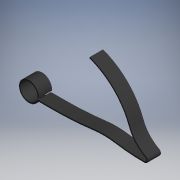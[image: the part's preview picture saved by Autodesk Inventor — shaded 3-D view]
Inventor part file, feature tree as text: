
AUTODESK INVENTOR PART (.ipt)
format: ipt  version: 2019 (Build 230136000, 136)  size: 154,624 bytes
history: native  units: mm (DEFAULTED — no unit token found)
features: extrude x1, sketch x1
ambient origin geometry x8: Origin, YZ Plane, XZ Plane, XY Plane, X Axis, Y Axis, Z Axis, Center Point
bodies: Solid1 (feature_tree)
feature tree (2):
  extrude  "Extrusion2"  Depth=1.3mm
  sketch  "Sketch1"  dims[d25=8.726646mm d26=7.40714mm d27=10.0mm d28=5.0mm d29=2.0mm d30=0.0mm d34=0.5mm d35=1.3mm d36=16.0mm]
